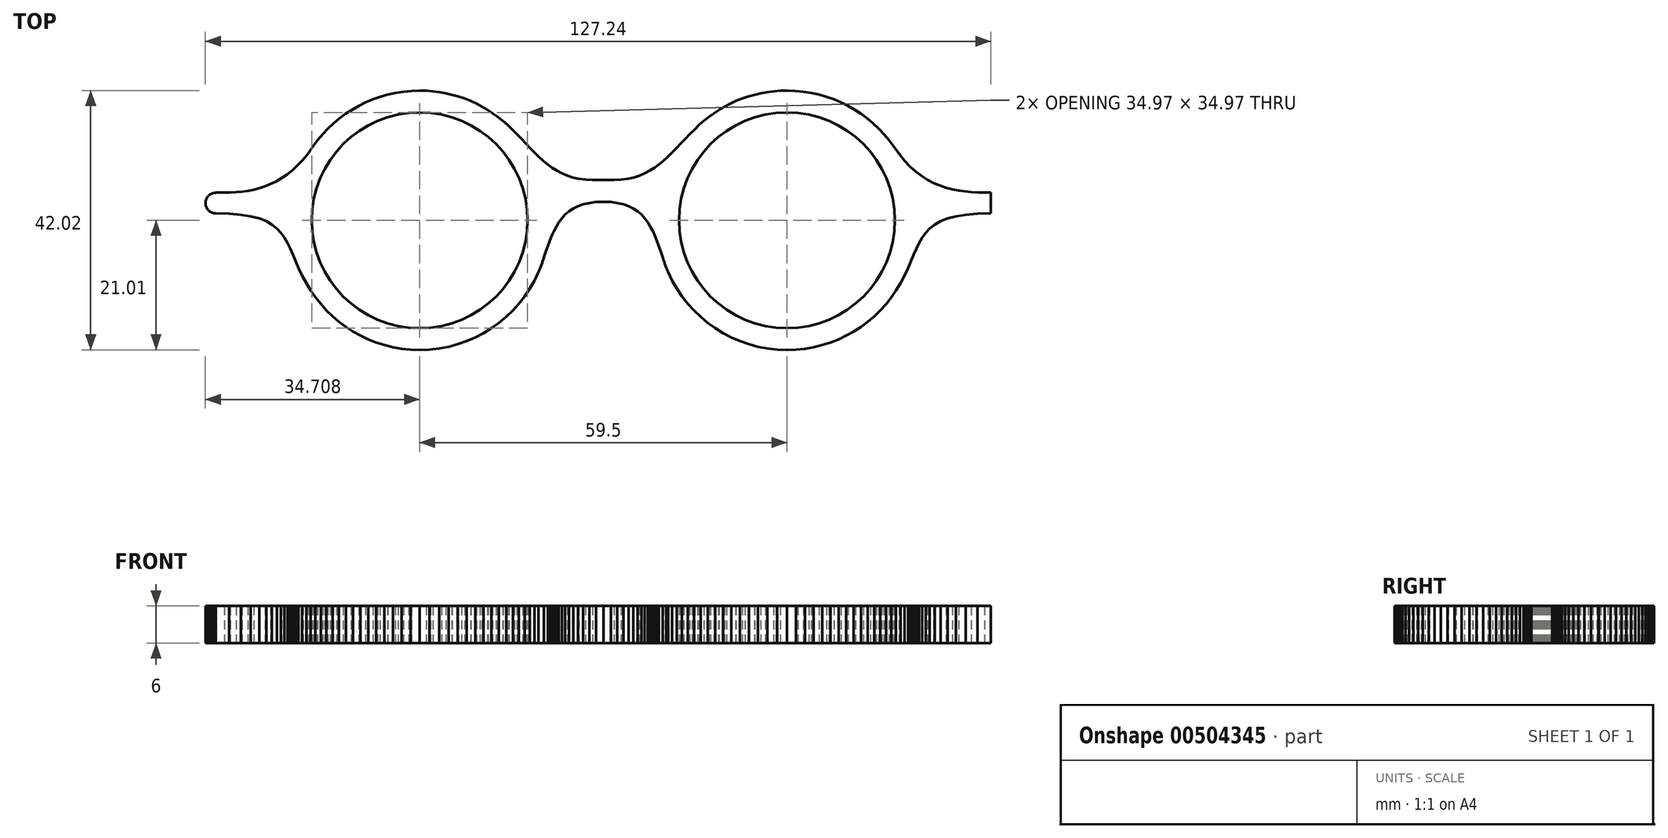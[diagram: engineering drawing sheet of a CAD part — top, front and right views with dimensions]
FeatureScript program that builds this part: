
annotation { "Feature Type Name" : "Feature", "Feature Type Description" : "" }
export const myFeature = defineFeature(function(context is Context, id is Id, definition is map)
    precondition{}
    {
        {
            var Q0;
            Q0=qCreatedBy(makeId("Top.planeOp"),FACE);
            var sketch = newSketch(context, id + "F0", { "sketchPlane" : qUnion([Q0])});
            skLineSegment(sketch, "E0", {"start": v(47.83, 11.99) * mm, "end": v(47.83, 12) * mm});
            skLineSegment(sketch, "E1", {"start": v(47.83, 12) * mm, "end": v(47.83, 12) * mm});
            skLineSegment(sketch, "E2", {"start": v(47.83, 12) * mm, "end": v(47.82, 12) * mm});
            skLineSegment(sketch, "E3", {"start": v(47.82, 12) * mm, "end": v(47.82, 12) * mm});
            skLineSegment(sketch, "E4", {"start": v(47.82, 12) * mm, "end": v(47.82, 12.01) * mm});
            skLineSegment(sketch, "E5", {"start": v(47.82, 12.01) * mm, "end": v(47.81, 12.01) * mm});
            skLineSegment(sketch, "E6", {"start": v(47.81, 12.01) * mm, "end": v(47.81, 12.01) * mm});
            skLineSegment(sketch, "E7", {"start": v(47.81, 12.01) * mm, "end": v(47.82, 12.01) * mm});
            skLineSegment(sketch, "E8", {"start": v(47.82, 12.01) * mm, "end": v(47.82, 12) * mm});
            skLineSegment(sketch, "E9", {"start": v(47.82, 12) * mm, "end": v(47.83, 12) * mm});
            skLineSegment(sketch, "E10", {"start": v(47.83, 12) * mm, "end": v(47.83, 11.99) * mm});
            skLineSegment(sketch, "E11", {"start": v(47.83, 11.99) * mm, "end": v(47.83, 11.99) * mm});
            skLineSegment(sketch, "E12", {"start": v(-46.15, 12) * mm, "end": v(-46.14, 12) * mm});
            skLineSegment(sketch, "E13", {"start": v(-46.14, 12) * mm, "end": v(-46.14, 12.01) * mm});
            skLineSegment(sketch, "E14", {"start": v(-46.14, 12.01) * mm, "end": v(-46.14, 12.01) * mm});
            skLineSegment(sketch, "E15", {"start": v(-46.14, 12.01) * mm, "end": v(-46.14, 12) * mm});
            skLineSegment(sketch, "E16", {"start": v(-46.14, 12) * mm, "end": v(-46.15, 12) * mm});
            skLineSegment(sketch, "E17", {"start": v(-46.15, 12) * mm, "end": v(-46.15, 12) * mm});
            skLineSegment(sketch, "E18", {"start": v(-46.15, 12) * mm, "end": v(-46.16, 12) * mm});
            skLineSegment(sketch, "E19", {"start": v(-46.16, 12) * mm, "end": v(-46.16, 11.99) * mm});
            skLineSegment(sketch, "E20", {"start": v(-46.16, 11.99) * mm, "end": v(-46.16, 11.99) * mm});
            skLineSegment(sketch, "E21", {"start": v(-46.16, 11.99) * mm, "end": v(-46.15, 12) * mm});
            skLineSegment(sketch, "E22", {"start": v(62.55, 4.48) * mm, "end": v(61.5, 4.5) * mm});
            skLineSegment(sketch, "E23", {"start": v(61.5, 4.5) * mm, "end": v(60.45, 4.57) * mm});
            skLineSegment(sketch, "E24", {"start": v(60.45, 4.57) * mm, "end": v(59.41, 4.67) * mm});
            skLineSegment(sketch, "E25", {"start": v(59.41, 4.67) * mm, "end": v(58.38, 4.82) * mm});
            skLineSegment(sketch, "E26", {"start": v(58.38, 4.82) * mm, "end": v(57.36, 5.02) * mm});
            skLineSegment(sketch, "E27", {"start": v(57.36, 5.02) * mm, "end": v(56.35, 5.29) * mm});
            skLineSegment(sketch, "E28", {"start": v(56.35, 5.29) * mm, "end": v(55.35, 5.62) * mm});
            skLineSegment(sketch, "E29", {"start": v(55.35, 5.62) * mm, "end": v(54.36, 6.05) * mm});
            skLineSegment(sketch, "E30", {"start": v(54.36, 6.05) * mm, "end": v(53.38, 6.56) * mm});
            skLineSegment(sketch, "E31", {"start": v(53.38, 6.56) * mm, "end": v(52.42, 7.17) * mm});
            skLineSegment(sketch, "E32", {"start": v(52.42, 7.17) * mm, "end": v(51.47, 7.88) * mm});
            skLineSegment(sketch, "E33", {"start": v(51.47, 7.88) * mm, "end": v(50.54, 8.71) * mm});
            skLineSegment(sketch, "E34", {"start": v(50.54, 8.71) * mm, "end": v(49.62, 9.67) * mm});
            skLineSegment(sketch, "E35", {"start": v(49.62, 9.67) * mm, "end": v(48.72, 10.76) * mm});
            skLineSegment(sketch, "E36", {"start": v(48.72, 10.76) * mm, "end": v(47.83, 11.99) * mm});
            skLineSegment(sketch, "E37", {"start": v(47.83, 11.99) * mm, "end": v(47.1, 12.99) * mm});
            skLineSegment(sketch, "E38", {"start": v(47.1, 12.99) * mm, "end": v(46.3, 13.94) * mm});
            skLineSegment(sketch, "E39", {"start": v(46.3, 13.94) * mm, "end": v(45.44, 14.84) * mm});
            skLineSegment(sketch, "E40", {"start": v(45.44, 14.84) * mm, "end": v(44.54, 15.7) * mm});
            skLineSegment(sketch, "E41", {"start": v(44.54, 15.7) * mm, "end": v(43.59, 16.5) * mm});
            skLineSegment(sketch, "E42", {"start": v(43.59, 16.5) * mm, "end": v(42.59, 17.24) * mm});
            skLineSegment(sketch, "E43", {"start": v(42.59, 17.24) * mm, "end": v(41.54, 17.92) * mm});
            skLineSegment(sketch, "E44", {"start": v(41.54, 17.92) * mm, "end": v(40.46, 18.54) * mm});
            skLineSegment(sketch, "E45", {"start": v(40.46, 18.54) * mm, "end": v(39.34, 19.1) * mm});
            skLineSegment(sketch, "E46", {"start": v(39.34, 19.1) * mm, "end": v(38.18, 19.6) * mm});
            skLineSegment(sketch, "E47", {"start": v(38.18, 19.6) * mm, "end": v(36.98, 20.02) * mm});
            skLineSegment(sketch, "E48", {"start": v(36.98, 20.02) * mm, "end": v(35.76, 20.37) * mm});
            skLineSegment(sketch, "E49", {"start": v(35.76, 20.37) * mm, "end": v(34.5, 20.65) * mm});
            skLineSegment(sketch, "E50", {"start": v(34.5, 20.65) * mm, "end": v(33.22, 20.85) * mm});
            skLineSegment(sketch, "E51", {"start": v(33.22, 20.85) * mm, "end": v(31.91, 20.97) * mm});
            skLineSegment(sketch, "E52", {"start": v(31.91, 20.97) * mm, "end": v(30.59, 21.01) * mm});
            skLineSegment(sketch, "E53", {"start": v(30.59, 21.01) * mm, "end": v(29.5, 20.99) * mm});
            skLineSegment(sketch, "E54", {"start": v(29.5, 20.99) * mm, "end": v(28.42, 20.9) * mm});
            skLineSegment(sketch, "E55", {"start": v(28.42, 20.9) * mm, "end": v(27.36, 20.77) * mm});
            skLineSegment(sketch, "E56", {"start": v(27.36, 20.77) * mm, "end": v(26.32, 20.58) * mm});
            skLineSegment(sketch, "E57", {"start": v(26.32, 20.58) * mm, "end": v(25.3, 20.34) * mm});
            skLineSegment(sketch, "E58", {"start": v(25.3, 20.34) * mm, "end": v(24.3, 20.05) * mm});
            skLineSegment(sketch, "E59", {"start": v(24.3, 20.05) * mm, "end": v(23.31, 19.71) * mm});
            skLineSegment(sketch, "E60", {"start": v(23.31, 19.71) * mm, "end": v(22.35, 19.33) * mm});
            skLineSegment(sketch, "E61", {"start": v(22.35, 19.33) * mm, "end": v(21.41, 18.9) * mm});
            skLineSegment(sketch, "E62", {"start": v(21.41, 18.9) * mm, "end": v(20.5, 18.43) * mm});
            skLineSegment(sketch, "E63", {"start": v(20.5, 18.43) * mm, "end": v(19.62, 17.92) * mm});
            skLineSegment(sketch, "E64", {"start": v(19.62, 17.92) * mm, "end": v(18.76, 17.36) * mm});
            skLineSegment(sketch, "E65", {"start": v(18.76, 17.36) * mm, "end": v(17.93, 16.76) * mm});
            skLineSegment(sketch, "E66", {"start": v(17.93, 16.76) * mm, "end": v(17.14, 16.13) * mm});
            skLineSegment(sketch, "E67", {"start": v(17.14, 16.13) * mm, "end": v(16.37, 15.46) * mm});
            skLineSegment(sketch, "E68", {"start": v(16.37, 15.46) * mm, "end": v(15.64, 14.75) * mm});
            skLineSegment(sketch, "E69", {"start": v(15.64, 14.75) * mm, "end": v(14.85, 13.97) * mm});
            skLineSegment(sketch, "E70", {"start": v(14.85, 13.97) * mm, "end": v(14.1, 13.2) * mm});
            skLineSegment(sketch, "E71", {"start": v(14.1, 13.2) * mm, "end": v(13.38, 12.44) * mm});
            skLineSegment(sketch, "E72", {"start": v(13.38, 12.44) * mm, "end": v(12.67, 11.7) * mm});
            skLineSegment(sketch, "E73", {"start": v(12.67, 11.7) * mm, "end": v(11.98, 10.99) * mm});
            skLineSegment(sketch, "E74", {"start": v(11.98, 10.99) * mm, "end": v(11.28, 10.3) * mm});
            skLineSegment(sketch, "E75", {"start": v(11.28, 10.3) * mm, "end": v(10.58, 9.67) * mm});
            skLineSegment(sketch, "E76", {"start": v(10.58, 9.67) * mm, "end": v(9.87, 9.07) * mm});
            skLineSegment(sketch, "E77", {"start": v(9.87, 9.07) * mm, "end": v(9.13, 8.52) * mm});
            skLineSegment(sketch, "E78", {"start": v(9.13, 8.52) * mm, "end": v(8.35, 8.03) * mm});
            skLineSegment(sketch, "E79", {"start": v(8.35, 8.03) * mm, "end": v(7.54, 7.6) * mm});
            skLineSegment(sketch, "E80", {"start": v(7.54, 7.6) * mm, "end": v(6.68, 7.23) * mm});
            skLineSegment(sketch, "E81", {"start": v(6.68, 7.23) * mm, "end": v(5.77, 6.93) * mm});
            skLineSegment(sketch, "E82", {"start": v(5.77, 6.93) * mm, "end": v(4.78, 6.71) * mm});
            skLineSegment(sketch, "E83", {"start": v(4.78, 6.71) * mm, "end": v(3.73, 6.58) * mm});
            skLineSegment(sketch, "E84", {"start": v(3.73, 6.58) * mm, "end": v(2.6, 6.53) * mm});
            skLineSegment(sketch, "E85", {"start": v(2.6, 6.53) * mm, "end": v(2.37, 6.53) * mm});
            skLineSegment(sketch, "E86", {"start": v(2.37, 6.53) * mm, "end": v(2.15, 6.53) * mm});
            skLineSegment(sketch, "E87", {"start": v(2.15, 6.53) * mm, "end": v(1.93, 6.53) * mm});
            skLineSegment(sketch, "E88", {"start": v(1.93, 6.53) * mm, "end": v(1.71, 6.53) * mm});
            skLineSegment(sketch, "E89", {"start": v(1.71, 6.53) * mm, "end": v(1.5, 6.53) * mm});
            skLineSegment(sketch, "E90", {"start": v(1.5, 6.53) * mm, "end": v(1.28, 6.53) * mm});
            skLineSegment(sketch, "E91", {"start": v(1.28, 6.53) * mm, "end": v(1.06, 6.53) * mm});
            skLineSegment(sketch, "E92", {"start": v(1.06, 6.53) * mm, "end": v(0.84, 6.53) * mm});
            skLineSegment(sketch, "E93", {"start": v(0.84, 6.53) * mm, "end": v(0.62, 6.53) * mm});
            skLineSegment(sketch, "E94", {"start": v(0.62, 6.53) * mm, "end": v(0.4, 6.53) * mm});
            skLineSegment(sketch, "E95", {"start": v(0.4, 6.53) * mm, "end": v(0.18, 6.53) * mm});
            skLineSegment(sketch, "E96", {"start": v(0.18, 6.53) * mm, "end": v(-0.04, 6.53) * mm});
            skLineSegment(sketch, "E97", {"start": v(-0.04, 6.53) * mm, "end": v(-0.26, 6.53) * mm});
            skLineSegment(sketch, "E98", {"start": v(-0.26, 6.53) * mm, "end": v(-0.48, 6.53) * mm});
            skLineSegment(sketch, "E99", {"start": v(-0.48, 6.53) * mm, "end": v(-0.7, 6.53) * mm});
            skLineSegment(sketch, "E100", {"start": v(-0.7, 6.53) * mm, "end": v(-0.92, 6.53) * mm});
            skLineSegment(sketch, "E101", {"start": v(-0.92, 6.53) * mm, "end": v(-2.05, 6.58) * mm});
            skLineSegment(sketch, "E102", {"start": v(-2.05, 6.58) * mm, "end": v(-3.1, 6.71) * mm});
            skLineSegment(sketch, "E103", {"start": v(-3.1, 6.71) * mm, "end": v(-4.1, 6.93) * mm});
            skLineSegment(sketch, "E104", {"start": v(-4.1, 6.93) * mm, "end": v(-5, 7.23) * mm});
            skLineSegment(sketch, "E105", {"start": v(-5, 7.23) * mm, "end": v(-5.87, 7.6) * mm});
            skLineSegment(sketch, "E106", {"start": v(-5.87, 7.6) * mm, "end": v(-6.68, 8.03) * mm});
            skLineSegment(sketch, "E107", {"start": v(-6.68, 8.03) * mm, "end": v(-7.45, 8.52) * mm});
            skLineSegment(sketch, "E108", {"start": v(-7.45, 8.52) * mm, "end": v(-8.2, 9.07) * mm});
            skLineSegment(sketch, "E109", {"start": v(-8.2, 9.07) * mm, "end": v(-8.9, 9.67) * mm});
            skLineSegment(sketch, "E110", {"start": v(-8.9, 9.67) * mm, "end": v(-9.6, 10.3) * mm});
            skLineSegment(sketch, "E111", {"start": v(-9.6, 10.3) * mm, "end": v(-10.3, 10.99) * mm});
            skLineSegment(sketch, "E112", {"start": v(-10.3, 10.99) * mm, "end": v(-11, 11.7) * mm});
            skLineSegment(sketch, "E113", {"start": v(-11, 11.7) * mm, "end": v(-11.7, 12.44) * mm});
            skLineSegment(sketch, "E114", {"start": v(-11.7, 12.44) * mm, "end": v(-12.43, 13.2) * mm});
            skLineSegment(sketch, "E115", {"start": v(-12.43, 13.2) * mm, "end": v(-13.18, 13.97) * mm});
            skLineSegment(sketch, "E116", {"start": v(-13.18, 13.97) * mm, "end": v(-13.96, 14.75) * mm});
            skLineSegment(sketch, "E117", {"start": v(-13.96, 14.75) * mm, "end": v(-14.7, 15.46) * mm});
            skLineSegment(sketch, "E118", {"start": v(-14.7, 15.46) * mm, "end": v(-15.46, 16.13) * mm});
            skLineSegment(sketch, "E119", {"start": v(-15.46, 16.13) * mm, "end": v(-16.26, 16.76) * mm});
            skLineSegment(sketch, "E120", {"start": v(-16.26, 16.76) * mm, "end": v(-17.09, 17.36) * mm});
            skLineSegment(sketch, "E121", {"start": v(-17.09, 17.36) * mm, "end": v(-17.94, 17.92) * mm});
            skLineSegment(sketch, "E122", {"start": v(-17.94, 17.92) * mm, "end": v(-18.83, 18.43) * mm});
            skLineSegment(sketch, "E123", {"start": v(-18.83, 18.43) * mm, "end": v(-19.74, 18.9) * mm});
            skLineSegment(sketch, "E124", {"start": v(-19.74, 18.9) * mm, "end": v(-20.68, 19.33) * mm});
            skLineSegment(sketch, "E125", {"start": v(-20.68, 19.33) * mm, "end": v(-21.64, 19.71) * mm});
            skLineSegment(sketch, "E126", {"start": v(-21.64, 19.71) * mm, "end": v(-22.62, 20.05) * mm});
            skLineSegment(sketch, "E127", {"start": v(-22.62, 20.05) * mm, "end": v(-23.62, 20.34) * mm});
            skLineSegment(sketch, "E128", {"start": v(-23.62, 20.34) * mm, "end": v(-24.65, 20.58) * mm});
            skLineSegment(sketch, "E129", {"start": v(-24.65, 20.58) * mm, "end": v(-25.69, 20.77) * mm});
            skLineSegment(sketch, "E130", {"start": v(-25.69, 20.77) * mm, "end": v(-26.75, 20.9) * mm});
            skLineSegment(sketch, "E131", {"start": v(-26.75, 20.9) * mm, "end": v(-27.82, 20.99) * mm});
            skLineSegment(sketch, "E132", {"start": v(-27.82, 20.99) * mm, "end": v(-28.91, 21.01) * mm});
            skLineSegment(sketch, "E133", {"start": v(-28.91, 21.01) * mm, "end": v(-30.24, 20.97) * mm});
            skLineSegment(sketch, "E134", {"start": v(-30.24, 20.97) * mm, "end": v(-31.55, 20.85) * mm});
            skLineSegment(sketch, "E135", {"start": v(-31.55, 20.85) * mm, "end": v(-32.83, 20.65) * mm});
            skLineSegment(sketch, "E136", {"start": v(-32.83, 20.65) * mm, "end": v(-34.08, 20.37) * mm});
            skLineSegment(sketch, "E137", {"start": v(-34.08, 20.37) * mm, "end": v(-35.3, 20.02) * mm});
            skLineSegment(sketch, "E138", {"start": v(-35.3, 20.02) * mm, "end": v(-36.5, 19.6) * mm});
            skLineSegment(sketch, "E139", {"start": v(-36.5, 19.6) * mm, "end": v(-37.66, 19.1) * mm});
            skLineSegment(sketch, "E140", {"start": v(-37.66, 19.1) * mm, "end": v(-38.78, 18.54) * mm});
            skLineSegment(sketch, "E141", {"start": v(-38.78, 18.54) * mm, "end": v(-39.87, 17.92) * mm});
            skLineSegment(sketch, "E142", {"start": v(-39.87, 17.92) * mm, "end": v(-40.91, 17.24) * mm});
            skLineSegment(sketch, "E143", {"start": v(-40.91, 17.24) * mm, "end": v(-41.91, 16.5) * mm});
            skLineSegment(sketch, "E144", {"start": v(-41.91, 16.5) * mm, "end": v(-42.86, 15.7) * mm});
            skLineSegment(sketch, "E145", {"start": v(-42.86, 15.7) * mm, "end": v(-43.77, 14.84) * mm});
            skLineSegment(sketch, "E146", {"start": v(-43.77, 14.84) * mm, "end": v(-44.62, 13.94) * mm});
            skLineSegment(sketch, "E147", {"start": v(-44.62, 13.94) * mm, "end": v(-45.42, 12.99) * mm});
            skLineSegment(sketch, "E148", {"start": v(-45.42, 12.99) * mm, "end": v(-46.16, 11.99) * mm});
            skLineSegment(sketch, "E149", {"start": v(-46.16, 11.99) * mm, "end": v(-46.97, 10.85) * mm});
            skLineSegment(sketch, "E150", {"start": v(-46.97, 10.85) * mm, "end": v(-47.8, 9.84) * mm});
            skLineSegment(sketch, "E151", {"start": v(-47.8, 9.84) * mm, "end": v(-48.64, 8.93) * mm});
            skLineSegment(sketch, "E152", {"start": v(-48.64, 8.93) * mm, "end": v(-49.5, 8.14) * mm});
            skLineSegment(sketch, "E153", {"start": v(-49.5, 8.14) * mm, "end": v(-50.36, 7.44) * mm});
            skLineSegment(sketch, "E154", {"start": v(-50.36, 7.44) * mm, "end": v(-51.24, 6.83) * mm});
            skLineSegment(sketch, "E155", {"start": v(-51.24, 6.83) * mm, "end": v(-52.13, 6.31) * mm});
            skLineSegment(sketch, "E156", {"start": v(-52.13, 6.31) * mm, "end": v(-53.03, 5.87) * mm});
            skLineSegment(sketch, "E157", {"start": v(-53.03, 5.87) * mm, "end": v(-53.95, 5.5) * mm});
            skLineSegment(sketch, "E158", {"start": v(-53.95, 5.5) * mm, "end": v(-54.87, 5.2) * mm});
            skLineSegment(sketch, "E159", {"start": v(-54.87, 5.2) * mm, "end": v(-55.8, 4.97) * mm});
            skLineSegment(sketch, "E160", {"start": v(-55.8, 4.97) * mm, "end": v(-56.73, 4.79) * mm});
            skLineSegment(sketch, "E161", {"start": v(-56.73, 4.79) * mm, "end": v(-57.68, 4.65) * mm});
            skLineSegment(sketch, "E162", {"start": v(-57.68, 4.65) * mm, "end": v(-58.63, 4.56) * mm});
            skLineSegment(sketch, "E163", {"start": v(-58.63, 4.56) * mm, "end": v(-59.58, 4.5) * mm});
            skLineSegment(sketch, "E164", {"start": v(-59.58, 4.5) * mm, "end": v(-60.54, 4.48) * mm});
            skLineSegment(sketch, "E165", {"start": v(-60.54, 4.48) * mm, "end": v(-60.63, 4.48) * mm});
            skLineSegment(sketch, "E166", {"start": v(-60.63, 4.48) * mm, "end": v(-60.72, 4.48) * mm});
            skLineSegment(sketch, "E167", {"start": v(-60.72, 4.48) * mm, "end": v(-60.8, 4.48) * mm});
            skLineSegment(sketch, "E168", {"start": v(-60.8, 4.48) * mm, "end": v(-60.9, 4.48) * mm});
            skLineSegment(sketch, "E169", {"start": v(-60.9, 4.48) * mm, "end": v(-60.98, 4.48) * mm});
            skLineSegment(sketch, "E170", {"start": v(-60.98, 4.48) * mm, "end": v(-61.07, 4.48) * mm});
            skLineSegment(sketch, "E171", {"start": v(-61.07, 4.48) * mm, "end": v(-61.15, 4.48) * mm});
            skLineSegment(sketch, "E172", {"start": v(-61.15, 4.48) * mm, "end": v(-61.24, 4.47) * mm});
            skLineSegment(sketch, "E173", {"start": v(-61.24, 4.47) * mm, "end": v(-61.33, 4.47) * mm});
            skLineSegment(sketch, "E174", {"start": v(-61.33, 4.47) * mm, "end": v(-61.42, 4.47) * mm});
            skLineSegment(sketch, "E175", {"start": v(-61.42, 4.47) * mm, "end": v(-61.5, 4.47) * mm});
            skLineSegment(sketch, "E176", {"start": v(-61.5, 4.47) * mm, "end": v(-61.6, 4.47) * mm});
            skLineSegment(sketch, "E177", {"start": v(-61.6, 4.47) * mm, "end": v(-61.68, 4.47) * mm});
            skLineSegment(sketch, "E178", {"start": v(-61.68, 4.47) * mm, "end": v(-61.77, 4.47) * mm});
            skLineSegment(sketch, "E179", {"start": v(-61.77, 4.47) * mm, "end": v(-61.85, 4.47) * mm});
            skLineSegment(sketch, "E180", {"start": v(-61.85, 4.47) * mm, "end": v(-61.94, 4.47) * mm});
            skLineSegment(sketch, "E181", {"start": v(-61.94, 4.47) * mm, "end": v(-61.94, 4.47) * mm});
            skLineSegment(sketch, "E182", {"start": v(-61.94, 4.47) * mm, "end": v(-62.11, 4.46) * mm});
            skLineSegment(sketch, "E183", {"start": v(-62.11, 4.46) * mm, "end": v(-62.28, 4.44) * mm});
            skLineSegment(sketch, "E184", {"start": v(-62.28, 4.44) * mm, "end": v(-62.44, 4.4) * mm});
            skLineSegment(sketch, "E185", {"start": v(-62.44, 4.4) * mm, "end": v(-62.6, 4.34) * mm});
            skLineSegment(sketch, "E186", {"start": v(-62.6, 4.34) * mm, "end": v(-62.74, 4.27) * mm});
            skLineSegment(sketch, "E187", {"start": v(-62.74, 4.27) * mm, "end": v(-62.88, 4.18) * mm});
            skLineSegment(sketch, "E188", {"start": v(-62.88, 4.18) * mm, "end": v(-63, 4.09) * mm});
            skLineSegment(sketch, "E189", {"start": v(-63, 4.09) * mm, "end": v(-63.12, 3.98) * mm});
            skLineSegment(sketch, "E190", {"start": v(-63.12, 3.98) * mm, "end": v(-63.23, 3.86) * mm});
            skLineSegment(sketch, "E191", {"start": v(-63.23, 3.86) * mm, "end": v(-63.33, 3.73) * mm});
            skLineSegment(sketch, "E192", {"start": v(-63.33, 3.73) * mm, "end": v(-63.41, 3.6) * mm});
            skLineSegment(sketch, "E193", {"start": v(-63.41, 3.6) * mm, "end": v(-63.48, 3.45) * mm});
            skLineSegment(sketch, "E194", {"start": v(-63.48, 3.45) * mm, "end": v(-63.54, 3.3) * mm});
            skLineSegment(sketch, "E195", {"start": v(-63.54, 3.3) * mm, "end": v(-63.58, 3.13) * mm});
            skLineSegment(sketch, "E196", {"start": v(-63.58, 3.13) * mm, "end": v(-63.6, 2.97) * mm});
            skLineSegment(sketch, "E197", {"start": v(-63.6, 2.97) * mm, "end": v(-63.62, 2.8) * mm});
            skLineSegment(sketch, "E198", {"start": v(-63.62, 2.8) * mm, "end": v(-63.6, 2.62) * mm});
            skLineSegment(sketch, "E199", {"start": v(-63.6, 2.62) * mm, "end": v(-63.58, 2.46) * mm});
            skLineSegment(sketch, "E200", {"start": v(-63.58, 2.46) * mm, "end": v(-63.54, 2.3) * mm});
            skLineSegment(sketch, "E201", {"start": v(-63.54, 2.3) * mm, "end": v(-63.48, 2.14) * mm});
            skLineSegment(sketch, "E202", {"start": v(-63.48, 2.14) * mm, "end": v(-63.41, 2) * mm});
            skLineSegment(sketch, "E203", {"start": v(-63.41, 2) * mm, "end": v(-63.33, 1.86) * mm});
            skLineSegment(sketch, "E204", {"start": v(-63.33, 1.86) * mm, "end": v(-63.23, 1.73) * mm});
            skLineSegment(sketch, "E205", {"start": v(-63.23, 1.73) * mm, "end": v(-63.12, 1.6) * mm});
            skLineSegment(sketch, "E206", {"start": v(-63.12, 1.6) * mm, "end": v(-63, 1.5) * mm});
            skLineSegment(sketch, "E207", {"start": v(-63, 1.5) * mm, "end": v(-62.88, 1.4) * mm});
            skLineSegment(sketch, "E208", {"start": v(-62.88, 1.4) * mm, "end": v(-62.74, 1.32) * mm});
            skLineSegment(sketch, "E209", {"start": v(-62.74, 1.32) * mm, "end": v(-62.6, 1.25) * mm});
            skLineSegment(sketch, "E210", {"start": v(-62.6, 1.25) * mm, "end": v(-62.44, 1.2) * mm});
            skLineSegment(sketch, "E211", {"start": v(-62.44, 1.2) * mm, "end": v(-62.28, 1.15) * mm});
            skLineSegment(sketch, "E212", {"start": v(-62.28, 1.15) * mm, "end": v(-62.11, 1.13) * mm});
            skLineSegment(sketch, "E213", {"start": v(-62.11, 1.13) * mm, "end": v(-61.94, 1.12) * mm});
            skLineSegment(sketch, "E214", {"start": v(-61.94, 1.12) * mm, "end": v(-61.94, 1.12) * mm});
            skLineSegment(sketch, "E215", {"start": v(-61.94, 1.12) * mm, "end": v(-59.76, 1.06) * mm});
            skLineSegment(sketch, "E216", {"start": v(-59.76, 1.06) * mm, "end": v(-57.88, 0.9) * mm});
            skLineSegment(sketch, "E217", {"start": v(-57.88, 0.9) * mm, "end": v(-56.28, 0.65) * mm});
            skLineSegment(sketch, "E218", {"start": v(-56.28, 0.65) * mm, "end": v(-54.92, 0.29) * mm});
            skLineSegment(sketch, "E219", {"start": v(-54.92, 0.29) * mm, "end": v(-53.78, -0.16) * mm});
            skLineSegment(sketch, "E220", {"start": v(-53.78, -0.16) * mm, "end": v(-52.82, -0.7) * mm});
            skLineSegment(sketch, "E221", {"start": v(-52.82, -0.7) * mm, "end": v(-52.03, -1.33) * mm});
            skLineSegment(sketch, "E222", {"start": v(-52.03, -1.33) * mm, "end": v(-51.37, -2.04) * mm});
            skLineSegment(sketch, "E223", {"start": v(-51.37, -2.04) * mm, "end": v(-50.8, -2.82) * mm});
            skLineSegment(sketch, "E224", {"start": v(-50.8, -2.82) * mm, "end": v(-50.32, -3.68) * mm});
            skLineSegment(sketch, "E225", {"start": v(-50.32, -3.68) * mm, "end": v(-49.88, -4.6) * mm});
            skLineSegment(sketch, "E226", {"start": v(-49.88, -4.6) * mm, "end": v(-49.45, -5.6) * mm});
            skLineSegment(sketch, "E227", {"start": v(-49.45, -5.6) * mm, "end": v(-49, -6.66) * mm});
            skLineSegment(sketch, "E228", {"start": v(-49, -6.66) * mm, "end": v(-48.52, -7.77) * mm});
            skLineSegment(sketch, "E229", {"start": v(-48.52, -7.77) * mm, "end": v(-47.96, -8.94) * mm});
            skLineSegment(sketch, "E230", {"start": v(-47.96, -8.94) * mm, "end": v(-47.3, -10.15) * mm});
            skLineSegment(sketch, "E231", {"start": v(-47.3, -10.15) * mm, "end": v(-46.6, -11.34) * mm});
            skLineSegment(sketch, "E232", {"start": v(-46.6, -11.34) * mm, "end": v(-45.8, -12.48) * mm});
            skLineSegment(sketch, "E233", {"start": v(-45.8, -12.48) * mm, "end": v(-44.95, -13.56) * mm});
            skLineSegment(sketch, "E234", {"start": v(-44.95, -13.56) * mm, "end": v(-44.03, -14.58) * mm});
            skLineSegment(sketch, "E235", {"start": v(-44.03, -14.58) * mm, "end": v(-43.04, -15.54) * mm});
            skLineSegment(sketch, "E236", {"start": v(-43.04, -15.54) * mm, "end": v(-42, -16.43) * mm});
            skLineSegment(sketch, "E237", {"start": v(-42, -16.43) * mm, "end": v(-40.89, -17.26) * mm});
            skLineSegment(sketch, "E238", {"start": v(-40.89, -17.26) * mm, "end": v(-39.73, -18) * mm});
            skLineSegment(sketch, "E239", {"start": v(-39.73, -18) * mm, "end": v(-38.52, -18.69) * mm});
            skLineSegment(sketch, "E240", {"start": v(-38.52, -18.69) * mm, "end": v(-37.26, -19.28) * mm});
            skLineSegment(sketch, "E241", {"start": v(-37.26, -19.28) * mm, "end": v(-35.96, -19.8) * mm});
            skLineSegment(sketch, "E242", {"start": v(-35.96, -19.8) * mm, "end": v(-34.62, -20.23) * mm});
            skLineSegment(sketch, "E243", {"start": v(-34.62, -20.23) * mm, "end": v(-33.24, -20.57) * mm});
            skLineSegment(sketch, "E244", {"start": v(-33.24, -20.57) * mm, "end": v(-31.83, -20.81) * mm});
            skLineSegment(sketch, "E245", {"start": v(-31.83, -20.81) * mm, "end": v(-30.38, -20.96) * mm});
            skLineSegment(sketch, "E246", {"start": v(-30.38, -20.96) * mm, "end": v(-28.91, -21.01) * mm});
            skLineSegment(sketch, "E247", {"start": v(-28.91, -21.01) * mm, "end": v(-27.31, -20.95) * mm});
            skLineSegment(sketch, "E248", {"start": v(-27.31, -20.95) * mm, "end": v(-25.75, -20.78) * mm});
            skLineSegment(sketch, "E249", {"start": v(-25.75, -20.78) * mm, "end": v(-24.22, -20.49) * mm});
            skLineSegment(sketch, "E250", {"start": v(-24.22, -20.49) * mm, "end": v(-22.73, -20.09) * mm});
            skLineSegment(sketch, "E251", {"start": v(-22.73, -20.09) * mm, "end": v(-21.3, -19.58) * mm});
            skLineSegment(sketch, "E252", {"start": v(-21.3, -19.58) * mm, "end": v(-19.9, -18.98) * mm});
            skLineSegment(sketch, "E253", {"start": v(-19.9, -18.98) * mm, "end": v(-18.56, -18.28) * mm});
            skLineSegment(sketch, "E254", {"start": v(-18.56, -18.28) * mm, "end": v(-17.28, -17.5) * mm});
            skLineSegment(sketch, "E255", {"start": v(-17.28, -17.5) * mm, "end": v(-16.06, -16.61) * mm});
            skLineSegment(sketch, "E256", {"start": v(-16.06, -16.61) * mm, "end": v(-14.91, -15.65) * mm});
            skLineSegment(sketch, "E257", {"start": v(-14.91, -15.65) * mm, "end": v(-13.83, -14.62) * mm});
            skLineSegment(sketch, "E258", {"start": v(-13.83, -14.62) * mm, "end": v(-12.83, -13.5) * mm});
            skLineSegment(sketch, "E259", {"start": v(-12.83, -13.5) * mm, "end": v(-11.9, -12.33) * mm});
            skLineSegment(sketch, "E260", {"start": v(-11.9, -12.33) * mm, "end": v(-11.07, -11.08) * mm});
            skLineSegment(sketch, "E261", {"start": v(-11.07, -11.08) * mm, "end": v(-10.32, -9.77) * mm});
            skLineSegment(sketch, "E262", {"start": v(-10.32, -9.77) * mm, "end": v(-9.66, -8.4) * mm});
            skLineSegment(sketch, "E263", {"start": v(-9.66, -8.4) * mm, "end": v(-9.6, -8.26) * mm});
            skLineSegment(sketch, "E264", {"start": v(-9.6, -8.26) * mm, "end": v(-9.53, -8.11) * mm});
            skLineSegment(sketch, "E265", {"start": v(-9.53, -8.11) * mm, "end": v(-9.47, -7.96) * mm});
            skLineSegment(sketch, "E266", {"start": v(-9.47, -7.96) * mm, "end": v(-9.41, -7.81) * mm});
            skLineSegment(sketch, "E267", {"start": v(-9.41, -7.81) * mm, "end": v(-9.35, -7.66) * mm});
            skLineSegment(sketch, "E268", {"start": v(-9.35, -7.66) * mm, "end": v(-9.3, -7.5) * mm});
            skLineSegment(sketch, "E269", {"start": v(-9.3, -7.5) * mm, "end": v(-9.23, -7.35) * mm});
            skLineSegment(sketch, "E270", {"start": v(-9.23, -7.35) * mm, "end": v(-9.18, -7.2) * mm});
            skLineSegment(sketch, "E271", {"start": v(-9.18, -7.2) * mm, "end": v(-9.12, -7.04) * mm});
            skLineSegment(sketch, "E272", {"start": v(-9.12, -7.04) * mm, "end": v(-9.06, -6.89) * mm});
            skLineSegment(sketch, "E273", {"start": v(-9.06, -6.89) * mm, "end": v(-9.01, -6.73) * mm});
            skLineSegment(sketch, "E274", {"start": v(-9.01, -6.73) * mm, "end": v(-8.96, -6.57) * mm});
            skLineSegment(sketch, "E275", {"start": v(-8.96, -6.57) * mm, "end": v(-8.9, -6.42) * mm});
            skLineSegment(sketch, "E276", {"start": v(-8.9, -6.42) * mm, "end": v(-8.86, -6.26) * mm});
            skLineSegment(sketch, "E277", {"start": v(-8.86, -6.26) * mm, "end": v(-8.8, -6.1) * mm});
            skLineSegment(sketch, "E278", {"start": v(-8.8, -6.1) * mm, "end": v(-8.76, -5.95) * mm});
            skLineSegment(sketch, "E279", {"start": v(-8.76, -5.95) * mm, "end": v(-8.45, -5.05) * mm});
            skLineSegment(sketch, "E280", {"start": v(-8.45, -5.05) * mm, "end": v(-8.15, -4.18) * mm});
            skLineSegment(sketch, "E281", {"start": v(-8.15, -4.18) * mm, "end": v(-7.84, -3.33) * mm});
            skLineSegment(sketch, "E282", {"start": v(-7.84, -3.33) * mm, "end": v(-7.51, -2.51) * mm});
            skLineSegment(sketch, "E283", {"start": v(-7.51, -2.51) * mm, "end": v(-7.16, -1.73) * mm});
            skLineSegment(sketch, "E284", {"start": v(-7.16, -1.73) * mm, "end": v(-6.77, -1) * mm});
            skLineSegment(sketch, "E285", {"start": v(-6.77, -1) * mm, "end": v(-6.35, -0.3) * mm});
            skLineSegment(sketch, "E286", {"start": v(-6.35, -0.3) * mm, "end": v(-5.87, 0.34) * mm});
            skLineSegment(sketch, "E287", {"start": v(-5.87, 0.34) * mm, "end": v(-5.33, 0.93) * mm});
            skLineSegment(sketch, "E288", {"start": v(-5.33, 0.93) * mm, "end": v(-4.73, 1.45) * mm});
            skLineSegment(sketch, "E289", {"start": v(-4.73, 1.45) * mm, "end": v(-4.04, 1.9) * mm});
            skLineSegment(sketch, "E290", {"start": v(-4.04, 1.9) * mm, "end": v(-3.28, 2.29) * mm});
            skLineSegment(sketch, "E291", {"start": v(-3.28, 2.29) * mm, "end": v(-2.41, 2.6) * mm});
            skLineSegment(sketch, "E292", {"start": v(-2.41, 2.6) * mm, "end": v(-1.44, 2.82) * mm});
            skLineSegment(sketch, "E293", {"start": v(-1.44, 2.82) * mm, "end": v(-0.36, 2.96) * mm});
            skLineSegment(sketch, "E294", {"start": v(-0.36, 2.96) * mm, "end": v(0.84, 3) * mm});
            skLineSegment(sketch, "E295", {"start": v(0.84, 3) * mm, "end": v(2.04, 2.96) * mm});
            skLineSegment(sketch, "E296", {"start": v(2.04, 2.96) * mm, "end": v(3.12, 2.82) * mm});
            skLineSegment(sketch, "E297", {"start": v(3.12, 2.82) * mm, "end": v(4.09, 2.6) * mm});
            skLineSegment(sketch, "E298", {"start": v(4.09, 2.6) * mm, "end": v(4.95, 2.29) * mm});
            skLineSegment(sketch, "E299", {"start": v(4.95, 2.29) * mm, "end": v(5.72, 1.9) * mm});
            skLineSegment(sketch, "E300", {"start": v(5.72, 1.9) * mm, "end": v(6.4, 1.45) * mm});
            skLineSegment(sketch, "E301", {"start": v(6.4, 1.45) * mm, "end": v(7, 0.93) * mm});
            skLineSegment(sketch, "E302", {"start": v(7, 0.93) * mm, "end": v(7.55, 0.34) * mm});
            skLineSegment(sketch, "E303", {"start": v(7.55, 0.34) * mm, "end": v(8.02, -0.3) * mm});
            skLineSegment(sketch, "E304", {"start": v(8.02, -0.3) * mm, "end": v(8.45, -1) * mm});
            skLineSegment(sketch, "E305", {"start": v(8.45, -1) * mm, "end": v(8.83, -1.73) * mm});
            skLineSegment(sketch, "E306", {"start": v(8.83, -1.73) * mm, "end": v(9.19, -2.51) * mm});
            skLineSegment(sketch, "E307", {"start": v(9.19, -2.51) * mm, "end": v(9.51, -3.33) * mm});
            skLineSegment(sketch, "E308", {"start": v(9.51, -3.33) * mm, "end": v(9.82, -4.18) * mm});
            skLineSegment(sketch, "E309", {"start": v(9.82, -4.18) * mm, "end": v(10.13, -5.05) * mm});
            skLineSegment(sketch, "E310", {"start": v(10.13, -5.05) * mm, "end": v(10.44, -5.95) * mm});
            skLineSegment(sketch, "E311", {"start": v(10.44, -5.95) * mm, "end": v(10.48, -6.1) * mm});
            skLineSegment(sketch, "E312", {"start": v(10.48, -6.1) * mm, "end": v(10.53, -6.26) * mm});
            skLineSegment(sketch, "E313", {"start": v(10.53, -6.26) * mm, "end": v(10.58, -6.42) * mm});
            skLineSegment(sketch, "E314", {"start": v(10.58, -6.42) * mm, "end": v(10.63, -6.57) * mm});
            skLineSegment(sketch, "E315", {"start": v(10.63, -6.57) * mm, "end": v(10.69, -6.73) * mm});
            skLineSegment(sketch, "E316", {"start": v(10.69, -6.73) * mm, "end": v(10.74, -6.89) * mm});
            skLineSegment(sketch, "E317", {"start": v(10.74, -6.89) * mm, "end": v(10.8, -7.04) * mm});
            skLineSegment(sketch, "E318", {"start": v(10.8, -7.04) * mm, "end": v(10.85, -7.2) * mm});
            skLineSegment(sketch, "E319", {"start": v(10.85, -7.2) * mm, "end": v(10.9, -7.35) * mm});
            skLineSegment(sketch, "E320", {"start": v(10.9, -7.35) * mm, "end": v(10.97, -7.5) * mm});
            skLineSegment(sketch, "E321", {"start": v(10.97, -7.5) * mm, "end": v(11.02, -7.66) * mm});
            skLineSegment(sketch, "E322", {"start": v(11.02, -7.66) * mm, "end": v(11.09, -7.81) * mm});
            skLineSegment(sketch, "E323", {"start": v(11.09, -7.81) * mm, "end": v(11.15, -7.96) * mm});
            skLineSegment(sketch, "E324", {"start": v(11.15, -7.96) * mm, "end": v(11.2, -8.11) * mm});
            skLineSegment(sketch, "E325", {"start": v(11.2, -8.11) * mm, "end": v(11.27, -8.26) * mm});
            skLineSegment(sketch, "E326", {"start": v(11.27, -8.26) * mm, "end": v(11.34, -8.4) * mm});
            skLineSegment(sketch, "E327", {"start": v(11.34, -8.4) * mm, "end": v(12, -9.77) * mm});
            skLineSegment(sketch, "E328", {"start": v(12, -9.77) * mm, "end": v(12.74, -11.08) * mm});
            skLineSegment(sketch, "E329", {"start": v(12.74, -11.08) * mm, "end": v(13.58, -12.33) * mm});
            skLineSegment(sketch, "E330", {"start": v(13.58, -12.33) * mm, "end": v(14.5, -13.5) * mm});
            skLineSegment(sketch, "E331", {"start": v(14.5, -13.5) * mm, "end": v(15.5, -14.62) * mm});
            skLineSegment(sketch, "E332", {"start": v(15.5, -14.62) * mm, "end": v(16.59, -15.65) * mm});
            skLineSegment(sketch, "E333", {"start": v(16.59, -15.65) * mm, "end": v(17.74, -16.61) * mm});
            skLineSegment(sketch, "E334", {"start": v(17.74, -16.61) * mm, "end": v(18.96, -17.5) * mm});
            skLineSegment(sketch, "E335", {"start": v(18.96, -17.5) * mm, "end": v(20.24, -18.28) * mm});
            skLineSegment(sketch, "E336", {"start": v(20.24, -18.28) * mm, "end": v(21.57, -18.98) * mm});
            skLineSegment(sketch, "E337", {"start": v(21.57, -18.98) * mm, "end": v(22.97, -19.58) * mm});
            skLineSegment(sketch, "E338", {"start": v(22.97, -19.58) * mm, "end": v(24.4, -20.09) * mm});
            skLineSegment(sketch, "E339", {"start": v(24.4, -20.09) * mm, "end": v(25.9, -20.49) * mm});
            skLineSegment(sketch, "E340", {"start": v(25.9, -20.49) * mm, "end": v(27.43, -20.78) * mm});
            skLineSegment(sketch, "E341", {"start": v(27.43, -20.78) * mm, "end": v(29, -20.95) * mm});
            skLineSegment(sketch, "E342", {"start": v(29, -20.95) * mm, "end": v(30.59, -21.01) * mm});
            skLineSegment(sketch, "E343", {"start": v(30.59, -21.01) * mm, "end": v(32.06, -20.96) * mm});
            skLineSegment(sketch, "E344", {"start": v(32.06, -20.96) * mm, "end": v(33.5, -20.81) * mm});
            skLineSegment(sketch, "E345", {"start": v(33.5, -20.81) * mm, "end": v(34.91, -20.57) * mm});
            skLineSegment(sketch, "E346", {"start": v(34.91, -20.57) * mm, "end": v(36.3, -20.23) * mm});
            skLineSegment(sketch, "E347", {"start": v(36.3, -20.23) * mm, "end": v(37.63, -19.8) * mm});
            skLineSegment(sketch, "E348", {"start": v(37.63, -19.8) * mm, "end": v(38.93, -19.29) * mm});
            skLineSegment(sketch, "E349", {"start": v(38.93, -19.29) * mm, "end": v(40.2, -18.69) * mm});
            skLineSegment(sketch, "E350", {"start": v(40.2, -18.69) * mm, "end": v(41.4, -18.01) * mm});
            skLineSegment(sketch, "E351", {"start": v(41.4, -18.01) * mm, "end": v(42.56, -17.26) * mm});
            skLineSegment(sketch, "E352", {"start": v(42.56, -17.26) * mm, "end": v(43.67, -16.44) * mm});
            skLineSegment(sketch, "E353", {"start": v(43.67, -16.44) * mm, "end": v(44.71, -15.54) * mm});
            skLineSegment(sketch, "E354", {"start": v(44.71, -15.54) * mm, "end": v(45.7, -14.59) * mm});
            skLineSegment(sketch, "E355", {"start": v(45.7, -14.59) * mm, "end": v(46.62, -13.57) * mm});
            skLineSegment(sketch, "E356", {"start": v(46.62, -13.57) * mm, "end": v(47.48, -12.49) * mm});
            skLineSegment(sketch, "E357", {"start": v(47.48, -12.49) * mm, "end": v(48.27, -11.35) * mm});
            skLineSegment(sketch, "E358", {"start": v(48.27, -11.35) * mm, "end": v(48.98, -10.16) * mm});
            skLineSegment(sketch, "E359", {"start": v(48.98, -10.16) * mm, "end": v(49.63, -8.94) * mm});
            skLineSegment(sketch, "E360", {"start": v(49.63, -8.94) * mm, "end": v(50.2, -7.78) * mm});
            skLineSegment(sketch, "E361", {"start": v(50.2, -7.78) * mm, "end": v(50.68, -6.66) * mm});
            skLineSegment(sketch, "E362", {"start": v(50.68, -6.66) * mm, "end": v(51.12, -5.6) * mm});
            skLineSegment(sketch, "E363", {"start": v(51.12, -5.6) * mm, "end": v(51.55, -4.61) * mm});
            skLineSegment(sketch, "E364", {"start": v(51.55, -4.61) * mm, "end": v(52, -3.68) * mm});
            skLineSegment(sketch, "E365", {"start": v(52, -3.68) * mm, "end": v(52.48, -2.82) * mm});
            skLineSegment(sketch, "E366", {"start": v(52.48, -2.82) * mm, "end": v(53.04, -2.04) * mm});
            skLineSegment(sketch, "E367", {"start": v(53.04, -2.04) * mm, "end": v(53.7, -1.33) * mm});
            skLineSegment(sketch, "E368", {"start": v(53.7, -1.33) * mm, "end": v(54.5, -0.7) * mm});
            skLineSegment(sketch, "E369", {"start": v(54.5, -0.7) * mm, "end": v(55.45, -0.16) * mm});
            skLineSegment(sketch, "E370", {"start": v(55.45, -0.16) * mm, "end": v(56.6, 0.29) * mm});
            skLineSegment(sketch, "E371", {"start": v(56.6, 0.29) * mm, "end": v(57.95, 0.64) * mm});
            skLineSegment(sketch, "E372", {"start": v(57.95, 0.64) * mm, "end": v(59.55, 0.9) * mm});
            skLineSegment(sketch, "E373", {"start": v(59.55, 0.9) * mm, "end": v(61.43, 1.06) * mm});
            skLineSegment(sketch, "E374", {"start": v(61.43, 1.06) * mm, "end": v(63.62, 1.12) * mm});
            skLineSegment(sketch, "E375", {"start": v(63.62, 1.12) * mm, "end": v(63.62, 1.5) * mm});
            skLineSegment(sketch, "E376", {"start": v(63.62, 1.5) * mm, "end": v(63.62, 1.8) * mm});
            skLineSegment(sketch, "E377", {"start": v(63.62, 1.8) * mm, "end": v(63.62, 2.06) * mm});
            skLineSegment(sketch, "E378", {"start": v(63.62, 2.06) * mm, "end": v(63.62, 2.26) * mm});
            skLineSegment(sketch, "E379", {"start": v(63.62, 2.26) * mm, "end": v(63.62, 2.44) * mm});
            skLineSegment(sketch, "E380", {"start": v(63.62, 2.44) * mm, "end": v(63.62, 2.58) * mm});
            skLineSegment(sketch, "E381", {"start": v(63.62, 2.58) * mm, "end": v(63.62, 2.7) * mm});
            skLineSegment(sketch, "E382", {"start": v(63.62, 2.7) * mm, "end": v(63.62, 2.82) * mm});
            skLineSegment(sketch, "E383", {"start": v(63.62, 2.82) * mm, "end": v(63.62, 2.94) * mm});
            skLineSegment(sketch, "E384", {"start": v(63.62, 2.94) * mm, "end": v(63.62, 3.06) * mm});
            skLineSegment(sketch, "E385", {"start": v(63.62, 3.06) * mm, "end": v(63.62, 3.2) * mm});
            skLineSegment(sketch, "E386", {"start": v(63.62, 3.2) * mm, "end": v(63.62, 3.37) * mm});
            skLineSegment(sketch, "E387", {"start": v(63.62, 3.37) * mm, "end": v(63.62, 3.57) * mm});
            skLineSegment(sketch, "E388", {"start": v(63.62, 3.57) * mm, "end": v(63.62, 3.81) * mm});
            skLineSegment(sketch, "E389", {"start": v(63.62, 3.81) * mm, "end": v(63.62, 4.11) * mm});
            skLineSegment(sketch, "E390", {"start": v(63.62, 4.11) * mm, "end": v(63.62, 4.47) * mm});
            skLineSegment(sketch, "E391", {"start": v(63.62, 4.47) * mm, "end": v(62.55, 4.48) * mm});
            skLineSegment(sketch, "E392", {"start": v(-11.52, -1.79) * mm, "end": v(-11.78, -3.52) * mm});
            skLineSegment(sketch, "E393", {"start": v(-11.78, -3.52) * mm, "end": v(-12.21, -5.2) * mm});
            skLineSegment(sketch, "E394", {"start": v(-12.21, -5.2) * mm, "end": v(-12.8, -6.8) * mm});
            skLineSegment(sketch, "E395", {"start": v(-12.8, -6.8) * mm, "end": v(-13.54, -8.33) * mm});
            skLineSegment(sketch, "E396", {"start": v(-13.54, -8.33) * mm, "end": v(-14.42, -9.77) * mm});
            skLineSegment(sketch, "E397", {"start": v(-14.42, -9.77) * mm, "end": v(-15.42, -11.12) * mm});
            skLineSegment(sketch, "E398", {"start": v(-15.42, -11.12) * mm, "end": v(-16.55, -12.36) * mm});
            skLineSegment(sketch, "E399", {"start": v(-16.55, -12.36) * mm, "end": v(-17.8, -13.49) * mm});
            skLineSegment(sketch, "E400", {"start": v(-17.8, -13.49) * mm, "end": v(-19.14, -14.5) * mm});
            skLineSegment(sketch, "E401", {"start": v(-19.14, -14.5) * mm, "end": v(-20.58, -15.37) * mm});
            skLineSegment(sketch, "E402", {"start": v(-20.58, -15.37) * mm, "end": v(-22.11, -16.1) * mm});
            skLineSegment(sketch, "E403", {"start": v(-22.11, -16.1) * mm, "end": v(-23.72, -16.7) * mm});
            skLineSegment(sketch, "E404", {"start": v(-23.72, -16.7) * mm, "end": v(-25.4, -17.13) * mm});
            skLineSegment(sketch, "E405", {"start": v(-25.4, -17.13) * mm, "end": v(-27.13, -17.4) * mm});
            skLineSegment(sketch, "E406", {"start": v(-27.13, -17.4) * mm, "end": v(-28.91, -17.49) * mm});
            skLineSegment(sketch, "E407", {"start": v(-28.91, -17.49) * mm, "end": v(-30.7, -17.4) * mm});
            skLineSegment(sketch, "E408", {"start": v(-30.7, -17.4) * mm, "end": v(-32.43, -17.13) * mm});
            skLineSegment(sketch, "E409", {"start": v(-32.43, -17.13) * mm, "end": v(-34.1, -16.7) * mm});
            skLineSegment(sketch, "E410", {"start": v(-34.1, -16.7) * mm, "end": v(-35.71, -16.1) * mm});
            skLineSegment(sketch, "E411", {"start": v(-35.71, -16.1) * mm, "end": v(-37.24, -15.37) * mm});
            skLineSegment(sketch, "E412", {"start": v(-37.24, -15.37) * mm, "end": v(-38.68, -14.5) * mm});
            skLineSegment(sketch, "E413", {"start": v(-38.68, -14.5) * mm, "end": v(-40.03, -13.49) * mm});
            skLineSegment(sketch, "E414", {"start": v(-40.03, -13.49) * mm, "end": v(-41.27, -12.36) * mm});
            skLineSegment(sketch, "E415", {"start": v(-41.27, -12.36) * mm, "end": v(-42.4, -11.12) * mm});
            skLineSegment(sketch, "E416", {"start": v(-42.4, -11.12) * mm, "end": v(-43.4, -9.77) * mm});
            skLineSegment(sketch, "E417", {"start": v(-43.4, -9.77) * mm, "end": v(-44.28, -8.33) * mm});
            skLineSegment(sketch, "E418", {"start": v(-44.28, -8.33) * mm, "end": v(-45.02, -6.8) * mm});
            skLineSegment(sketch, "E419", {"start": v(-45.02, -6.8) * mm, "end": v(-45.61, -5.2) * mm});
            skLineSegment(sketch, "E420", {"start": v(-45.61, -5.2) * mm, "end": v(-46.04, -3.52) * mm});
            skLineSegment(sketch, "E421", {"start": v(-46.04, -3.52) * mm, "end": v(-46.3, -1.79) * mm});
            skLineSegment(sketch, "E422", {"start": v(-46.3, -1.79) * mm, "end": v(-46.4, 0) * mm});
            skLineSegment(sketch, "E423", {"start": v(-46.4, 0) * mm, "end": v(-46.3, 1.79) * mm});
            skLineSegment(sketch, "E424", {"start": v(-46.3, 1.79) * mm, "end": v(-46.04, 3.52) * mm});
            skLineSegment(sketch, "E425", {"start": v(-46.04, 3.52) * mm, "end": v(-45.61, 5.2) * mm});
            skLineSegment(sketch, "E426", {"start": v(-45.61, 5.2) * mm, "end": v(-45.02, 6.8) * mm});
            skLineSegment(sketch, "E427", {"start": v(-45.02, 6.8) * mm, "end": v(-44.28, 8.33) * mm});
            skLineSegment(sketch, "E428", {"start": v(-44.28, 8.33) * mm, "end": v(-43.4, 9.77) * mm});
            skLineSegment(sketch, "E429", {"start": v(-43.4, 9.77) * mm, "end": v(-42.4, 11.12) * mm});
            skLineSegment(sketch, "E430", {"start": v(-42.4, 11.12) * mm, "end": v(-41.27, 12.36) * mm});
            skLineSegment(sketch, "E431", {"start": v(-41.27, 12.36) * mm, "end": v(-40.03, 13.49) * mm});
            skLineSegment(sketch, "E432", {"start": v(-40.03, 13.49) * mm, "end": v(-38.68, 14.5) * mm});
            skLineSegment(sketch, "E433", {"start": v(-38.68, 14.5) * mm, "end": v(-37.24, 15.37) * mm});
            skLineSegment(sketch, "E434", {"start": v(-37.24, 15.37) * mm, "end": v(-35.71, 16.1) * mm});
            skLineSegment(sketch, "E435", {"start": v(-35.71, 16.1) * mm, "end": v(-34.1, 16.7) * mm});
            skLineSegment(sketch, "E436", {"start": v(-34.1, 16.7) * mm, "end": v(-32.43, 17.13) * mm});
            skLineSegment(sketch, "E437", {"start": v(-32.43, 17.13) * mm, "end": v(-30.7, 17.4) * mm});
            skLineSegment(sketch, "E438", {"start": v(-30.7, 17.4) * mm, "end": v(-28.91, 17.49) * mm});
            skLineSegment(sketch, "E439", {"start": v(-28.91, 17.49) * mm, "end": v(-27.13, 17.4) * mm});
            skLineSegment(sketch, "E440", {"start": v(-27.13, 17.4) * mm, "end": v(-25.4, 17.13) * mm});
            skLineSegment(sketch, "E441", {"start": v(-25.4, 17.13) * mm, "end": v(-23.72, 16.7) * mm});
            skLineSegment(sketch, "E442", {"start": v(-23.72, 16.7) * mm, "end": v(-22.11, 16.1) * mm});
            skLineSegment(sketch, "E443", {"start": v(-22.11, 16.1) * mm, "end": v(-20.58, 15.37) * mm});
            skLineSegment(sketch, "E444", {"start": v(-20.58, 15.37) * mm, "end": v(-19.14, 14.5) * mm});
            skLineSegment(sketch, "E445", {"start": v(-19.14, 14.5) * mm, "end": v(-17.8, 13.49) * mm});
            skLineSegment(sketch, "E446", {"start": v(-17.8, 13.49) * mm, "end": v(-16.55, 12.36) * mm});
            skLineSegment(sketch, "E447", {"start": v(-16.55, 12.36) * mm, "end": v(-15.42, 11.12) * mm});
            skLineSegment(sketch, "E448", {"start": v(-15.42, 11.12) * mm, "end": v(-14.42, 9.77) * mm});
            skLineSegment(sketch, "E449", {"start": v(-14.42, 9.77) * mm, "end": v(-13.54, 8.33) * mm});
            skLineSegment(sketch, "E450", {"start": v(-13.54, 8.33) * mm, "end": v(-12.8, 6.8) * mm});
            skLineSegment(sketch, "E451", {"start": v(-12.8, 6.8) * mm, "end": v(-12.21, 5.2) * mm});
            skLineSegment(sketch, "E452", {"start": v(-12.21, 5.2) * mm, "end": v(-11.78, 3.52) * mm});
            skLineSegment(sketch, "E453", {"start": v(-11.78, 3.52) * mm, "end": v(-11.52, 1.79) * mm});
            skLineSegment(sketch, "E454", {"start": v(-11.52, 1.79) * mm, "end": v(-11.43, 0) * mm});
            skLineSegment(sketch, "E455", {"start": v(-11.43, 0) * mm, "end": v(-11.52, -1.79) * mm});
            skLineSegment(sketch, "E456", {"start": v(47.98, -1.79) * mm, "end": v(47.72, -3.52) * mm});
            skLineSegment(sketch, "E457", {"start": v(47.72, -3.52) * mm, "end": v(47.29, -5.2) * mm});
            skLineSegment(sketch, "E458", {"start": v(47.29, -5.2) * mm, "end": v(46.7, -6.8) * mm});
            skLineSegment(sketch, "E459", {"start": v(46.7, -6.8) * mm, "end": v(45.96, -8.33) * mm});
            skLineSegment(sketch, "E460", {"start": v(45.96, -8.33) * mm, "end": v(45.08, -9.77) * mm});
            skLineSegment(sketch, "E461", {"start": v(45.08, -9.77) * mm, "end": v(44.08, -11.12) * mm});
            skLineSegment(sketch, "E462", {"start": v(44.08, -11.12) * mm, "end": v(42.95, -12.36) * mm});
            skLineSegment(sketch, "E463", {"start": v(42.95, -12.36) * mm, "end": v(41.7, -13.49) * mm});
            skLineSegment(sketch, "E464", {"start": v(41.7, -13.49) * mm, "end": v(40.36, -14.5) * mm});
            skLineSegment(sketch, "E465", {"start": v(40.36, -14.5) * mm, "end": v(38.92, -15.37) * mm});
            skLineSegment(sketch, "E466", {"start": v(38.92, -15.37) * mm, "end": v(37.39, -16.1) * mm});
            skLineSegment(sketch, "E467", {"start": v(37.39, -16.1) * mm, "end": v(35.78, -16.7) * mm});
            skLineSegment(sketch, "E468", {"start": v(35.78, -16.7) * mm, "end": v(34.1, -17.13) * mm});
            skLineSegment(sketch, "E469", {"start": v(34.1, -17.13) * mm, "end": v(32.37, -17.4) * mm});
            skLineSegment(sketch, "E470", {"start": v(32.37, -17.4) * mm, "end": v(30.59, -17.49) * mm});
            skLineSegment(sketch, "E471", {"start": v(30.59, -17.49) * mm, "end": v(28.8, -17.4) * mm});
            skLineSegment(sketch, "E472", {"start": v(28.8, -17.4) * mm, "end": v(27.07, -17.13) * mm});
            skLineSegment(sketch, "E473", {"start": v(27.07, -17.13) * mm, "end": v(25.4, -16.7) * mm});
            skLineSegment(sketch, "E474", {"start": v(25.4, -16.7) * mm, "end": v(23.79, -16.1) * mm});
            skLineSegment(sketch, "E475", {"start": v(23.79, -16.1) * mm, "end": v(22.26, -15.37) * mm});
            skLineSegment(sketch, "E476", {"start": v(22.26, -15.37) * mm, "end": v(20.82, -14.5) * mm});
            skLineSegment(sketch, "E477", {"start": v(20.82, -14.5) * mm, "end": v(19.47, -13.49) * mm});
            skLineSegment(sketch, "E478", {"start": v(19.47, -13.49) * mm, "end": v(18.23, -12.36) * mm});
            skLineSegment(sketch, "E479", {"start": v(18.23, -12.36) * mm, "end": v(17.1, -11.12) * mm});
            skLineSegment(sketch, "E480", {"start": v(17.1, -11.12) * mm, "end": v(16.1, -9.77) * mm});
            skLineSegment(sketch, "E481", {"start": v(16.1, -9.77) * mm, "end": v(15.21, -8.33) * mm});
            skLineSegment(sketch, "E482", {"start": v(15.21, -8.33) * mm, "end": v(14.48, -6.8) * mm});
            skLineSegment(sketch, "E483", {"start": v(14.48, -6.8) * mm, "end": v(13.89, -5.2) * mm});
            skLineSegment(sketch, "E484", {"start": v(13.89, -5.2) * mm, "end": v(13.46, -3.52) * mm});
            skLineSegment(sketch, "E485", {"start": v(13.46, -3.52) * mm, "end": v(13.2, -1.79) * mm});
            skLineSegment(sketch, "E486", {"start": v(13.2, -1.79) * mm, "end": v(13.1, 0) * mm});
            skLineSegment(sketch, "E487", {"start": v(13.1, 0) * mm, "end": v(13.2, 1.79) * mm});
            skLineSegment(sketch, "E488", {"start": v(13.2, 1.79) * mm, "end": v(13.46, 3.52) * mm});
            skLineSegment(sketch, "E489", {"start": v(13.46, 3.52) * mm, "end": v(13.89, 5.2) * mm});
            skLineSegment(sketch, "E490", {"start": v(13.89, 5.2) * mm, "end": v(14.48, 6.8) * mm});
            skLineSegment(sketch, "E491", {"start": v(14.48, 6.8) * mm, "end": v(15.21, 8.33) * mm});
            skLineSegment(sketch, "E492", {"start": v(15.21, 8.33) * mm, "end": v(16.1, 9.77) * mm});
            skLineSegment(sketch, "E493", {"start": v(16.1, 9.77) * mm, "end": v(17.1, 11.12) * mm});
            skLineSegment(sketch, "E494", {"start": v(17.1, 11.12) * mm, "end": v(18.23, 12.36) * mm});
            skLineSegment(sketch, "E495", {"start": v(18.23, 12.36) * mm, "end": v(19.47, 13.49) * mm});
            skLineSegment(sketch, "E496", {"start": v(19.47, 13.49) * mm, "end": v(20.82, 14.5) * mm});
            skLineSegment(sketch, "E497", {"start": v(20.82, 14.5) * mm, "end": v(22.26, 15.37) * mm});
            skLineSegment(sketch, "E498", {"start": v(22.26, 15.37) * mm, "end": v(23.79, 16.1) * mm});
            skLineSegment(sketch, "E499", {"start": v(23.79, 16.1) * mm, "end": v(25.4, 16.7) * mm});
            skLineSegment(sketch, "E500", {"start": v(25.4, 16.7) * mm, "end": v(27.07, 17.13) * mm});
            skLineSegment(sketch, "E501", {"start": v(27.07, 17.13) * mm, "end": v(28.8, 17.4) * mm});
            skLineSegment(sketch, "E502", {"start": v(28.8, 17.4) * mm, "end": v(30.59, 17.49) * mm});
            skLineSegment(sketch, "E503", {"start": v(30.59, 17.49) * mm, "end": v(32.37, 17.4) * mm});
            skLineSegment(sketch, "E504", {"start": v(32.37, 17.4) * mm, "end": v(34.1, 17.13) * mm});
            skLineSegment(sketch, "E505", {"start": v(34.1, 17.13) * mm, "end": v(35.78, 16.7) * mm});
            skLineSegment(sketch, "E506", {"start": v(35.78, 16.7) * mm, "end": v(37.39, 16.1) * mm});
            skLineSegment(sketch, "E507", {"start": v(37.39, 16.1) * mm, "end": v(38.92, 15.37) * mm});
            skLineSegment(sketch, "E508", {"start": v(38.92, 15.37) * mm, "end": v(40.36, 14.5) * mm});
            skLineSegment(sketch, "E509", {"start": v(40.36, 14.5) * mm, "end": v(41.7, 13.49) * mm});
            skLineSegment(sketch, "E510", {"start": v(41.7, 13.49) * mm, "end": v(42.95, 12.36) * mm});
            skLineSegment(sketch, "E511", {"start": v(42.95, 12.36) * mm, "end": v(44.08, 11.12) * mm});
            skLineSegment(sketch, "E512", {"start": v(44.08, 11.12) * mm, "end": v(45.08, 9.77) * mm});
            skLineSegment(sketch, "E513", {"start": v(45.08, 9.77) * mm, "end": v(45.96, 8.33) * mm});
            skLineSegment(sketch, "E514", {"start": v(45.96, 8.33) * mm, "end": v(46.7, 6.8) * mm});
            skLineSegment(sketch, "E515", {"start": v(46.7, 6.8) * mm, "end": v(47.29, 5.2) * mm});
            skLineSegment(sketch, "E516", {"start": v(47.29, 5.2) * mm, "end": v(47.72, 3.52) * mm});
            skLineSegment(sketch, "E517", {"start": v(47.72, 3.52) * mm, "end": v(47.98, 1.79) * mm});
            skLineSegment(sketch, "E518", {"start": v(47.98, 1.79) * mm, "end": v(48.07, 0) * mm});
            skLineSegment(sketch, "E519", {"start": v(48.07, 0) * mm, "end": v(47.98, -1.79) * mm});
            skSolve(sketch);
        }
        {
            var Q0;
            Q0 = qSketchRegion(id + "F0", true);
            extrude(context, id + "F1", {"entities" : qUnion([Q0]), "depth" : 6 * mm});
        }
    });
